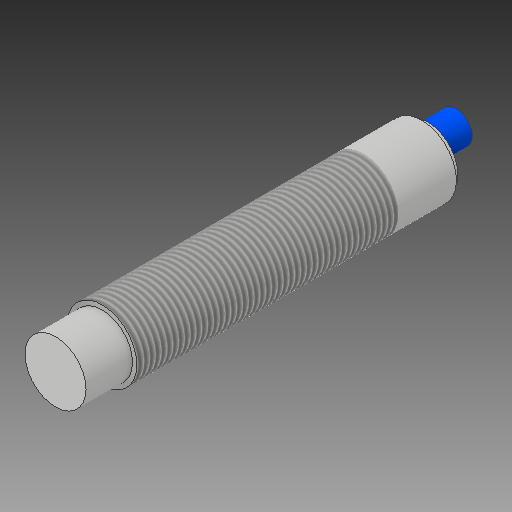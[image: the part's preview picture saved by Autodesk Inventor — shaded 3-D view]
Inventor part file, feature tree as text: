
AUTODESK INVENTOR PART (.ipt)
format: ipt  version: 2019 (Build 230136000, 136)  size: 182,272 bytes
history: native  units: mm
features: extrude x5, sketch x5, other x1, thread x1, fillet x1
ambient origin geometry x8: Origin, YZ Plane, XZ Plane, XY Plane, X Axis, Y Axis, Z Axis, Center Point
bodies: Body1 (feature_tree)
feature tree (13):
  other  "Твердое тело1"
  extrude  "Выдавливание1"  Depth=12.0mm
  extrude  "Выдавливание2"  Depth=55.0mm TaperAngle=0.0deg
  extrude  "Выдавливание3"  Depth=10.5mm
  thread  "Резьба1"
  extrude  "Выдавливание4"  Depth=8.0mm TaperAngle=0.0deg
  extrude  "Выдавливание5"  Depth=10.5mm
  fillet  "Сопряжение1"  Radius=1.0mm
  sketch  "Эскиз1"
  sketch  "Эскиз2"
  sketch  "Эскиз3"
  sketch  "Эскиз4"
  sketch  "Эскиз5"
